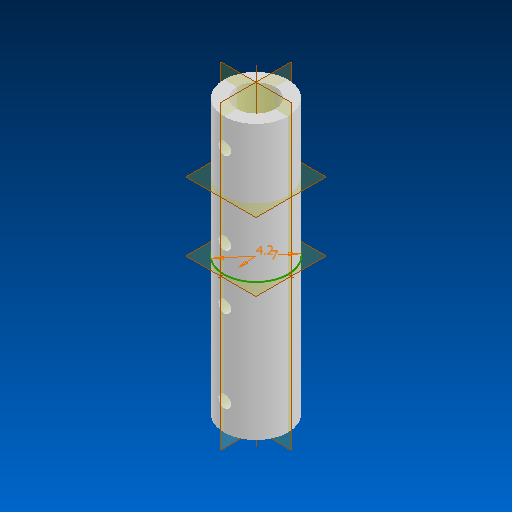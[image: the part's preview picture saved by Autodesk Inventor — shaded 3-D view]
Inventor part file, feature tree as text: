
AUTODESK INVENTOR PART (.ipt)
format: ipt  version: 2025 (Build 290162000, 162)  size: 113,152 bytes
history: native  units: mm
features: mirror x3, sketch x2, extrude x1, hole x1, plane x1
ambient origin geometry x8: Origin, YZ Plane, XZ Plane, XY Plane, X Axis, Y Axis, Z Axis, Center Point
bodies: Solid1 (feature_tree)
feature tree (8):
  extrude  "Extrusion1"  Depth=7.0mm
  hole  "Hole1"  [1 undecoded]
  plane  "Work Plane1"
  mirror  "Mirror1"
  mirror  "Mirror2"
  mirror  "Mirror3"
  sketch  "Sketch1"  dims[d0=4.2mm d1=7.0mm]
  sketch  "Sketch2"  dims[d2=15.0mm d3=0.0mm d4=1.4mm d5=6.0mm d6=3.023mm d7=2.0mm d8=14.3117mm d9=4.8mm d10=20.594885mm]
note: 1 required parameter value undecoded (feature->parameter linkage not recoverable at this tier; creation-order binding heuristic only, values carry confidence <= 0.55)
